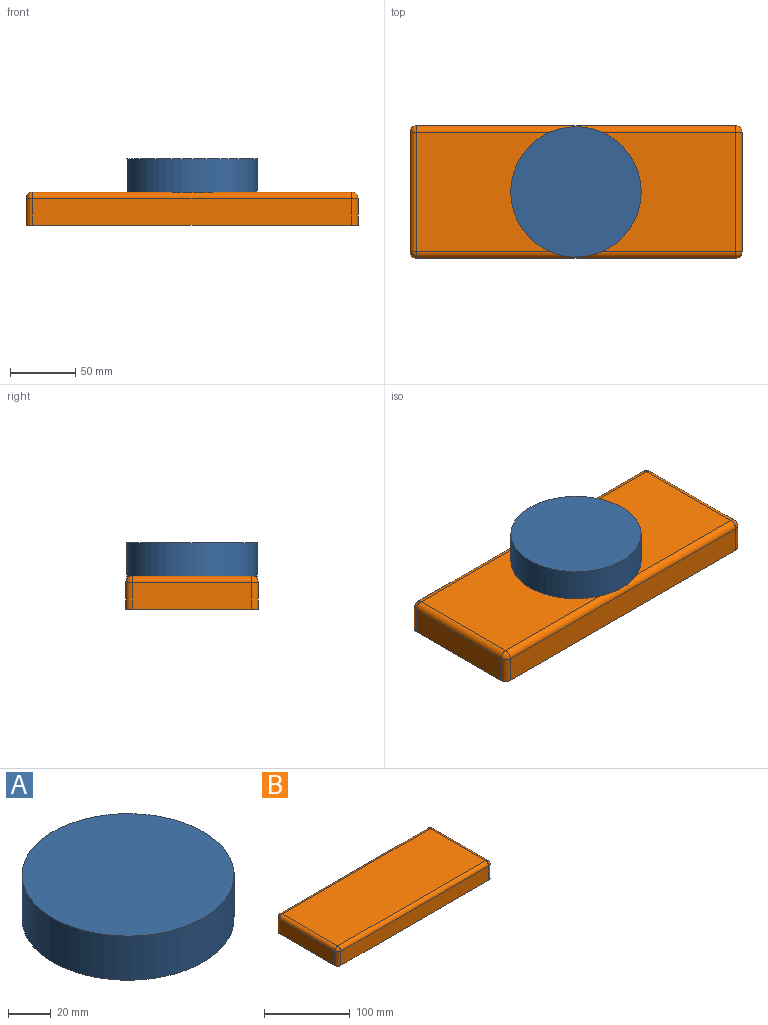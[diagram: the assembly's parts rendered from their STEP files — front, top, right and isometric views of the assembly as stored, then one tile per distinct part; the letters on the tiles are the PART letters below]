
ASSEMBLY  parts=2 mates=1
PART A: 3 faces, bbox 99.7x99.7x25.4 mm
  f0: cylinder r=49.85mm len=99.7mm, axis (0,0,-1), area 7955.7mm2, adj f1,f2
  f1: plane 99.7x99.7mm, normal (0,0,1), area 7807mm2, adj f0
  f2: plane 99.7x99.7mm, normal (0,0,-1), area 7807mm2, adj f0
PART B: 18 faces, bbox 254x101.6x25.4 mm
  f0: plane 243.84x20.32mm, normal (0,1,0), area 4954.8mm2, adj f5,f10,f14,f16
  f1: plane 91.44x20.32mm, normal (-1,0,0), area 1858.1mm2, adj f5,f7,f9,f16
  f2: plane 243.84x20.32mm, normal (0,-1,0), area 4954.8mm2, adj f5,f6,f7,f13
  f3: plane 91.44x20.32mm, normal (1,0,0), area 1858.1mm2, adj f5,f11,f13,f14
  f4: plane 243.84x91.44mm, normal (0,0,1), area 22296.7mm2, adj f6,f9,f10,f11
  f5: plane 254x101.6mm, normal (0,0,-1), area 25784.2mm2, adj f0,f1,f2,f3,f7,f13,f14,f16
  f6: cylinder r=5.08mm len=243.84mm, axis (-1,0,0), area 1945.8mm2, adj f2,f4,f8,f12
  f7: cylinder r=5.08mm len=20.32mm, axis (0,0,1), area 162.1mm2, adj f1,f2,f5,f8
  f8: sphere r=5.08mm, area 40.5mm2, adj f6,f7,f9
  f9: cylinder r=5.08mm len=91.44mm, axis (0,1,0), area 729.7mm2, adj f1,f4,f8,f17
  f10: cylinder r=5.08mm len=243.84mm, axis (1,0,0), area 1945.8mm2, adj f0,f4,f15,f17
  f11: cylinder r=5.08mm len=91.44mm, axis (0,-1,0), area 729.7mm2, adj f3,f4,f12,f15
  f12: sphere r=5.08mm, area 40.5mm2, adj f6,f11,f13
  f13: cylinder r=5.08mm len=20.32mm, axis (0,0,-1), area 162.1mm2, adj f2,f3,f5,f12
  f14: cylinder r=5.08mm len=20.32mm, axis (0,0,1), area 162.1mm2, adj f0,f3,f5,f15
  f15: sphere r=5.08mm, area 40.5mm2, adj f10,f11,f14
  f16: cylinder r=5.08mm len=20.32mm, axis (0,0,-1), area 162.1mm2, adj f0,f1,f5,f17
  f17: sphere r=5.08mm, area 40.5mm2, adj f9,f10,f16
PLACE A t=(-154.82,-110.66,-6.5)mm
PLACE B t=(-154.82,-110.66,-31.9)mm
MATE fastened A.f0 <-> B.f4  axis (0,0,-1) through (-154.82,-110.66,-6.5)mm
